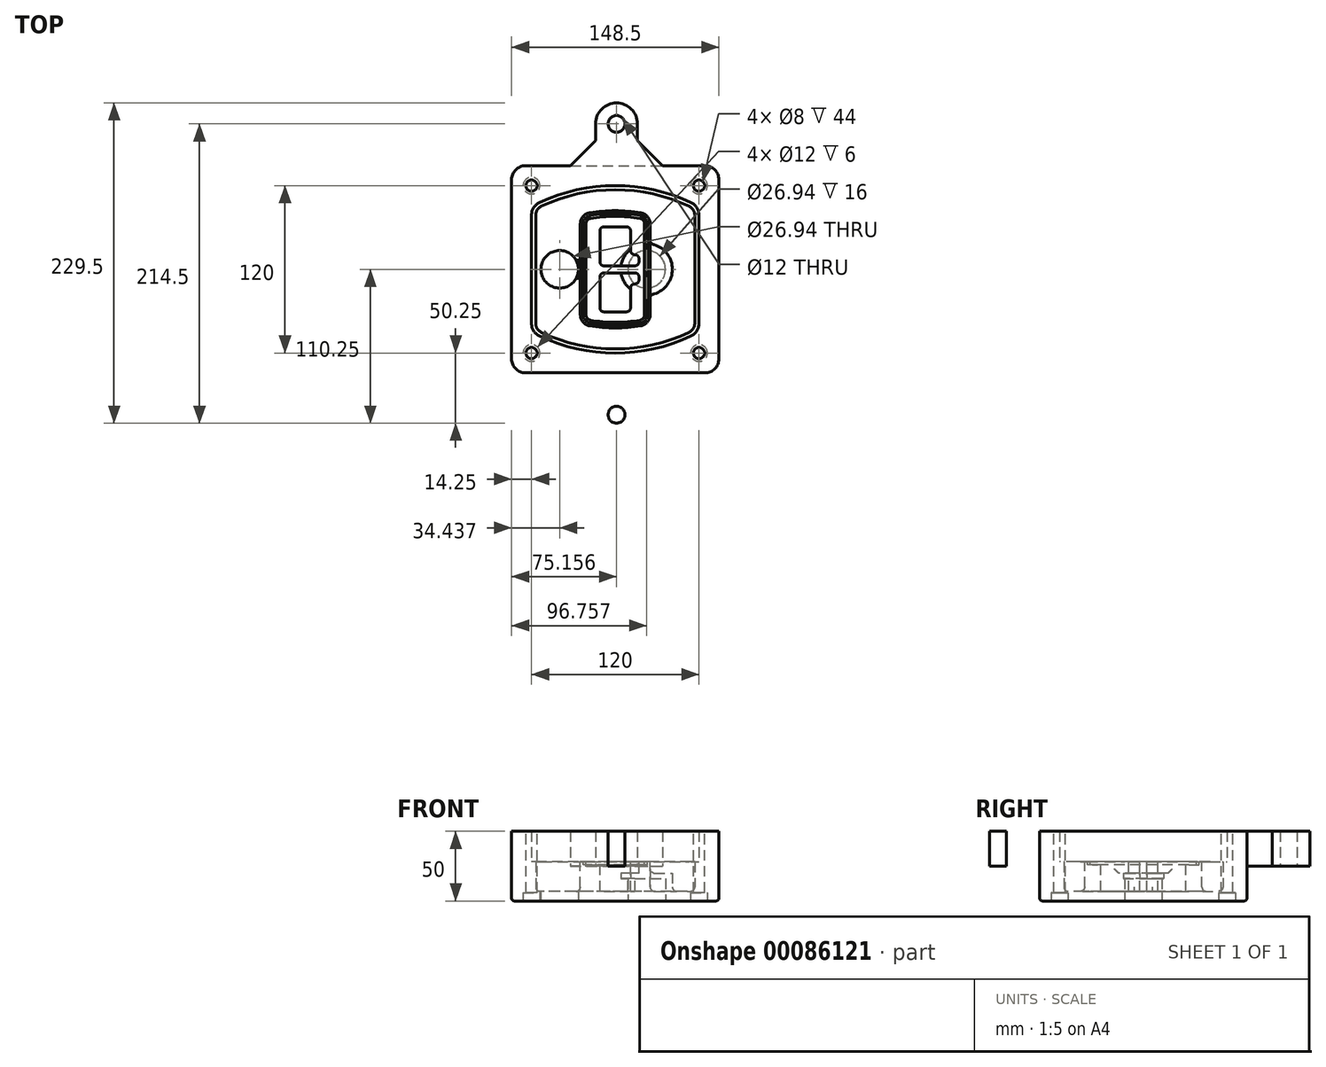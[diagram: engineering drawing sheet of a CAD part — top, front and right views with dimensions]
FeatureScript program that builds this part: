
annotation { "Feature Type Name" : "Feature", "Feature Type Description" : "" }
export const myFeature = defineFeature(function(context is Context, id is Id, definition is map)
    precondition{}
    {
        {
            var Q0;
            Q0=qCreatedBy(makeId("Top.planeOp"),FACE);
            var sketch = newSketch(context, id + "F0", { "sketchPlane" : qUnion([Q0])});
            skPoint(sketch, "E0.rect.middle", {"position": v(0, 0) * mm});
            skLineSegment(sketch, "E1.bottom", {"start": v(-64.25, -74.25) * mm, "end": v(64.25, -74.25) * mm});
            skLineSegment(sketch, "E1.top", {"start": v(-64.25, 74.25) * mm, "end": v(64.25, 74.25) * mm});
            skLineSegment(sketch, "E1.left", {"start": v(-74.25, -64.25) * mm, "end": v(-74.25, 64.25) * mm});
            skLineSegment(sketch, "E1.right", {"start": v(74.25, -64.25) * mm, "end": v(74.25, 64.25) * mm});
            skLineSegment(sketch, "E2", {"start": v(-74.25, 74.25) * mm, "end": v(74.25, -74.25) * mm, "construction": true});
            skLineSegment(sketch, "E3", {"start": v(74.25, 74.25) * mm, "end": v(-74.25, -74.25) * mm, "construction": true});
            skCircle(sketch, "E4", {"center": v(-60, 60) * mm, "radius": 4 * mm});
            skCircle(sketch, "E5", {"center": v(60, 60) * mm, "radius": 4 * mm});
            skCircle(sketch, "E6", {"center": v(60, -60) * mm, "radius": 4 * mm});
            skCircle(sketch, "E7", {"center": v(-60, -60) * mm, "radius": 4 * mm});
            skLineSegment(sketch, "E8", {"start": v(-60, 60) * mm, "end": v(60, 60) * mm, "construction": true});
            skLineSegment(sketch, "E9", {"start": v(60, 60) * mm, "end": v(60, -60) * mm, "construction": true});
            skLineSegment(sketch, "E10", {"start": v(60, -60) * mm, "end": v(-60, -60) * mm, "construction": true});
            skLineSegment(sketch, "E11", {"start": v(-60, -60) * mm, "end": v(-60, 60) * mm, "construction": true});
            skLineSegment(sketch, "E12", {"start": v(-60, 38.83) * mm, "end": v(-60, -38.83) * mm});
            skLineSegment(sketch, "E13", {"start": v(60, 38.83) * mm, "end": v(60, -38.83) * mm});
            skArc(sketch, "E14", {"start": v(54.26, 47.88) * mm, "mid": v(0, 60) * mm, "end": v(-54.26, 47.88) * mm});
            skArc(sketch, "E15", {"start": v(-54.26, -47.88) * mm, "mid": v(0, -60) * mm, "end": v(54.26, -47.88) * mm});
            skLineSegment(sketch, "E16", {"start": v(-60, 0) * mm, "end": v(60, 0) * mm, "construction": true});
            skPoint(sketch, "E17.visualSharp", {"position": v(-60, -45) * mm});
            skArc(sketch, "E17.filletArc", {"start": v(-60, -38.83) * mm, "mid": v(-58.44, -44.2) * mm, "end": v(-54.26, -47.88) * mm});
            skPoint(sketch, "E18.visualSharp", {"position": v(-60, 45) * mm});
            skArc(sketch, "E18.filletArc", {"start": v(-54.26, 47.88) * mm, "mid": v(-58.44, 44.2) * mm, "end": v(-60, 38.83) * mm});
            skPoint(sketch, "E19.visualSharp", {"position": v(60, 45) * mm});
            skArc(sketch, "E19.filletArc", {"start": v(60, 38.83) * mm, "mid": v(58.44, 44.2) * mm, "end": v(54.26, 47.88) * mm});
            skPoint(sketch, "E20.visualSharp", {"position": v(60, -45) * mm});
            skArc(sketch, "E20.filletArc", {"start": v(54.26, -47.88) * mm, "mid": v(58.44, -44.2) * mm, "end": v(60, -38.83) * mm});
            skPoint(sketch, "E21.visualSharp", {"position": v(-74.25, 74.25) * mm});
            skArc(sketch, "E21.filletArc", {"start": v(-64.25, 74.25) * mm, "mid": v(-71.32, 71.32) * mm, "end": v(-74.25, 64.25) * mm});
            skPoint(sketch, "E22.visualSharp", {"position": v(74.25, 74.25) * mm});
            skArc(sketch, "E22.filletArc", {"start": v(74.25, 64.25) * mm, "mid": v(71.32, 71.32) * mm, "end": v(64.25, 74.25) * mm});
            skPoint(sketch, "E23.visualSharp", {"position": v(74.25, -74.25) * mm});
            skArc(sketch, "E23.filletArc", {"start": v(64.25, -74.25) * mm, "mid": v(71.32, -71.32) * mm, "end": v(74.25, -64.25) * mm});
            skPoint(sketch, "E24.visualSharp", {"position": v(-74.25, -74.25) * mm});
            skArc(sketch, "E24.filletArc", {"start": v(-74.25, -64.25) * mm, "mid": v(-71.32, -71.32) * mm, "end": v(-64.25, -74.25) * mm});
            skArc(sketch, "E25.0", {"start": v(57, 38.83) * mm, "mid": v(55.9, 42.58) * mm, "end": v(52.98, 45.17) * mm});
            skLineSegment(sketch, "E25.1", {"start": v(57, 38.83) * mm, "end": v(57, -38.83) * mm});
            skArc(sketch, "E25.2", {"start": v(52.98, -45.17) * mm, "mid": v(55.9, -42.58) * mm, "end": v(57, -38.83) * mm});
            skArc(sketch, "E25.3", {"start": v(-52.98, -45.17) * mm, "mid": v(0, -57) * mm, "end": v(52.98, -45.17) * mm});
            skArc(sketch, "E25.4", {"start": v(-57, -38.83) * mm, "mid": v(-55.9, -42.58) * mm, "end": v(-52.98, -45.17) * mm});
            skArc(sketch, "E25.5", {"start": v(52.98, 45.17) * mm, "mid": v(0, 57) * mm, "end": v(-52.98, 45.17) * mm});
            skLineSegment(sketch, "E25.6", {"start": v(-57, 38.83) * mm, "end": v(-57, -38.83) * mm});
            skArc(sketch, "E25.7", {"start": v(-52.98, 45.17) * mm, "mid": v(-55.9, 42.58) * mm, "end": v(-57, 38.83) * mm});
            skArc(sketch, "E26.0", {"start": v(-55.96, 51.5) * mm, "mid": v(-61.82, 46.33) * mm, "end": v(-64, 38.83) * mm});
            skArc(sketch, "E26.1", {"start": v(55.96, 51.5) * mm, "mid": v(0, 64) * mm, "end": v(-55.96, 51.5) * mm});
            skArc(sketch, "E26.2", {"start": v(64, 38.83) * mm, "mid": v(61.82, 46.33) * mm, "end": v(55.96, 51.5) * mm});
            skLineSegment(sketch, "E26.3", {"start": v(64, 38.83) * mm, "end": v(64, -38.83) * mm});
            skArc(sketch, "E26.4", {"start": v(55.96, -51.5) * mm, "mid": v(61.82, -46.33) * mm, "end": v(64, -38.83) * mm});
            skLineSegment(sketch, "E26.5", {"start": v(-64, 38.83) * mm, "end": v(-64, -38.83) * mm});
            skArc(sketch, "E26.6", {"start": v(-55.96, -51.5) * mm, "mid": v(0, -64) * mm, "end": v(55.96, -51.5) * mm});
            skArc(sketch, "E26.7", {"start": v(-64, -38.83) * mm, "mid": v(-61.82, -46.33) * mm, "end": v(-55.96, -51.5) * mm});
            skSolve(sketch);
        }
        {
            var Q0;
            Q0=makeQuery(id+"F0.imprint","IMPRINT",FACE,{"disambiguationData":[TD([[makeQuery(id+"F0.imprint","IMPRINT",EDGE,{"derivedFrom":sQuery(id+"F0.wireOp",EDGE,"E1.bottom")}),1.0]])]});
            var Q1;
            Q1=makeQuery(id+"F0.imprint","IMPRINT",FACE,{"disambiguationData":[TD([[makeQuery(id+"F0.imprint","IMPRINT",EDGE,{"derivedFrom":sQuery(id+"F0.wireOp",EDGE,"E12")}),1.0]])]});
            var Q2;
            Q2=makeQuery(id+"F0.imprint","IMPRINT",FACE,{"disambiguationData":[TD([[makeQuery(id+"F0.imprint","IMPRINT",EDGE,{"derivedFrom":sQuery(id+"F0.wireOp",EDGE,"E25.0")}),1.0]])]});
            var Q3;
            Q3=makeQuery(id+"F0.imprint","IMPRINT",FACE,{"disambiguationData":[TD([[makeQuery(id+"F0.imprint","IMPRINT",EDGE,{"derivedFrom":sQuery(id+"F0.wireOp",EDGE,"E12")}),-1.0]])]});
            extrude(context, id + "F1", {"entities" : qUnion([Q0, Q1, Q2, Q3]), "oppositeDirection" : true, "depth" : 25 * mm});
        }
        {
            var Q0;
            Q0=makeQuery(id+"F0.imprint","IMPRINT",FACE,{"disambiguationData":[TD([[makeQuery(id+"F0.imprint","IMPRINT",EDGE,{"derivedFrom":sQuery(id+"F0.wireOp",EDGE,"E12")}),1.0]])]});
            extrude(context, id + "F2", {"entities" : qUnion([Q0]), "operationType" : NewBodyOperationType.ADD, "depth" : 3 * mm});
        }
        {
            var Q0;
            Q0=makeQuery(id+"F0.imprint","IMPRINT",FACE,{"disambiguationData":[TD([[makeQuery(id+"F0.imprint","IMPRINT",EDGE,{"derivedFrom":sQuery(id+"F0.wireOp",EDGE,"E25.0")}),1.0]])]});
            extrude(context, id + "F3", {"entities" : qUnion([Q0]), "operationType" : NewBodyOperationType.REMOVE, "oppositeDirection" : true, "depth" : 18 * mm});
        }
        {
            var Q0;
            Q0=makeQuery(id+"F2.opExtrude","CAP_FACE",FACE,{"disambiguationData":[OSD([sQuery(id+"F0.wireOp",EDGE,"E12"),sQuery(id+"F0.wireOp",EDGE,"E13"),sQuery(id+"F0.wireOp",EDGE,"E14"),sQuery(id+"F0.wireOp",EDGE,"E15"),sQuery(id+"F0.wireOp",EDGE,"E17.filletArc"),sQuery(id+"F0.wireOp",EDGE,"E18.filletArc"),sQuery(id+"F0.wireOp",EDGE,"E19.filletArc"),sQuery(id+"F0.wireOp",EDGE,"E20.filletArc"),sQuery(id+"F0.wireOp",EDGE,"E25.0"),sQuery(id+"F0.wireOp",EDGE,"E25.1"),sQuery(id+"F0.wireOp",EDGE,"E25.2"),sQuery(id+"F0.wireOp",EDGE,"E25.3"),sQuery(id+"F0.wireOp",EDGE,"E25.4"),sQuery(id+"F0.wireOp",EDGE,"E25.5"),sQuery(id+"F0.wireOp",EDGE,"E25.6"),sQuery(id+"F0.wireOp",EDGE,"E25.7")])],"isStart":false});
            var sketch = newSketch(context, id + "F4", { "sketchPlane" : qUnion([Q0])});
            skArc(sketch, "E27.0", {"start": v(-18.34, -40.45) * mm, "mid": v(0, -42) * mm, "end": v(18.34, -40.45) * mm});
            skArc(sketch, "E28.0", {"start": v(18.34, 40.45) * mm, "mid": v(0, 42) * mm, "end": v(-18.34, 40.45) * mm});
            skLineSegment(sketch, "E29", {"start": v(-25, 32.57) * mm, "end": v(-25, -32.57) * mm});
            skLineSegment(sketch, "E30", {"start": v(25, 32.57) * mm, "end": v(25, -32.57) * mm});
            skLineSegment(sketch, "E31", {"start": v(-25, 39.1) * mm, "end": v(25, 39.1) * mm, "construction": true});
            skLineSegment(sketch, "E32", {"start": v(-25, -39.1) * mm, "end": v(25, -39.1) * mm, "construction": true});
            skPoint(sketch, "E33.visualSharp", {"position": v(-25, 39.1) * mm});
            skArc(sketch, "E33.filletArc", {"start": v(-18.34, 40.45) * mm, "mid": v(-23.11, 37.73) * mm, "end": v(-25, 32.57) * mm});
            skPoint(sketch, "E34.visualSharp", {"position": v(25, 39.1) * mm});
            skArc(sketch, "E34.filletArc", {"start": v(25, 32.57) * mm, "mid": v(23.11, 37.73) * mm, "end": v(18.34, 40.45) * mm});
            skPoint(sketch, "E35.visualSharp", {"position": v(25, -39.1) * mm});
            skArc(sketch, "E35.filletArc", {"start": v(18.34, -40.45) * mm, "mid": v(23.11, -37.73) * mm, "end": v(25, -32.57) * mm});
            skPoint(sketch, "E36.visualSharp", {"position": v(-25, -39.1) * mm});
            skArc(sketch, "E36.filletArc", {"start": v(-25, -32.57) * mm, "mid": v(-23.11, -37.73) * mm, "end": v(-18.34, -40.45) * mm});
            skArc(sketch, "E37.0", {"start": v(52.98, 45.17) * mm, "mid": v(0, 57) * mm, "end": v(-52.98, 45.17) * mm});
            skArc(sketch, "E37.1", {"start": v(-52.98, 45.17) * mm, "mid": v(-55.9, 42.58) * mm, "end": v(-57, 38.83) * mm});
            skLineSegment(sketch, "E37.2", {"start": v(-57, 38.83) * mm, "end": v(-57, -38.83) * mm});
            skArc(sketch, "E37.3", {"start": v(-57, -38.83) * mm, "mid": v(-55.9, -42.58) * mm, "end": v(-52.98, -45.17) * mm});
            skArc(sketch, "E37.4", {"start": v(-52.98, -45.17) * mm, "mid": v(0, -57) * mm, "end": v(52.98, -45.17) * mm});
            skArc(sketch, "E37.5", {"start": v(52.98, -45.17) * mm, "mid": v(55.9, -42.58) * mm, "end": v(57, -38.83) * mm});
            skLineSegment(sketch, "E37.6", {"start": v(57, 38.83) * mm, "end": v(57, -38.83) * mm});
            skArc(sketch, "E37.7", {"start": v(57, 38.83) * mm, "mid": v(55.9, 42.58) * mm, "end": v(52.98, 45.17) * mm});
            skLineSegment(sketch, "E38.0", {"start": v(23, 32.57) * mm, "end": v(23, -32.57) * mm});
            skArc(sketch, "E38.1", {"start": v(18, -38.48) * mm, "mid": v(21.58, -36.44) * mm, "end": v(23, -32.57) * mm});
            skArc(sketch, "E38.2", {"start": v(-18, -38.48) * mm, "mid": v(0, -40) * mm, "end": v(18, -38.48) * mm});
            skArc(sketch, "E38.3", {"start": v(-23, -32.57) * mm, "mid": v(-21.58, -36.44) * mm, "end": v(-18, -38.48) * mm});
            skLineSegment(sketch, "E38.4", {"start": v(-23, 32.57) * mm, "end": v(-23, -32.57) * mm});
            skArc(sketch, "E38.5", {"start": v(23, 32.57) * mm, "mid": v(21.58, 36.44) * mm, "end": v(18, 38.48) * mm});
            skArc(sketch, "E38.6", {"start": v(-18, 38.48) * mm, "mid": v(-21.58, 36.44) * mm, "end": v(-23, 32.57) * mm});
            skArc(sketch, "E38.7", {"start": v(18, 38.48) * mm, "mid": v(0, 40) * mm, "end": v(-18, 38.48) * mm});
            skArc(sketch, "E39.0", {"start": v(21, 32.57) * mm, "mid": v(20.06, 35.15) * mm, "end": v(17.67, 36.5) * mm});
            skLineSegment(sketch, "E39.1", {"start": v(21, 32.57) * mm, "end": v(21, -32.57) * mm});
            skArc(sketch, "E39.2", {"start": v(17.67, -36.5) * mm, "mid": v(20.06, -35.15) * mm, "end": v(21, -32.57) * mm});
            skArc(sketch, "E39.3", {"start": v(-17.67, -36.5) * mm, "mid": v(0, -38) * mm, "end": v(17.67, -36.5) * mm});
            skArc(sketch, "E39.4", {"start": v(-21, -32.57) * mm, "mid": v(-20.06, -35.15) * mm, "end": v(-17.67, -36.5) * mm});
            skArc(sketch, "E39.5", {"start": v(17.67, 36.5) * mm, "mid": v(0, 38) * mm, "end": v(-17.67, 36.5) * mm});
            skLineSegment(sketch, "E39.6", {"start": v(-21, 32.57) * mm, "end": v(-21, -32.57) * mm});
            skArc(sketch, "E39.7", {"start": v(-17.67, 36.5) * mm, "mid": v(-20.06, 35.15) * mm, "end": v(-21, 32.57) * mm});
            skLineSegment(sketch, "E40", {"start": v(-25, 0) * mm, "end": v(25, 0) * mm, "construction": true});
            skLineSegment(sketch, "E41", {"start": v(-11, 5.5) * mm, "end": v(-11, 27.5) * mm});
            skLineSegment(sketch, "E42", {"start": v(-8, 30.5) * mm, "end": v(8, 30.5) * mm});
            skLineSegment(sketch, "E43", {"start": v(11, 27.5) * mm, "end": v(11, 13.5) * mm});
            skLineSegment(sketch, "E44", {"start": v(14, 10.5) * mm, "end": v(14, 10.5) * mm});
            skLineSegment(sketch, "E45", {"start": v(17, 7.5) * mm, "end": v(17, 5.5) * mm});
            skLineSegment(sketch, "E46", {"start": v(14, 2.5) * mm, "end": v(-8, 2.5) * mm});
            skPoint(sketch, "E47.visualSharp", {"position": v(-11, 30.5) * mm});
            skArc(sketch, "E47.filletArc", {"start": v(-8, 30.5) * mm, "mid": v(-10.12, 29.62) * mm, "end": v(-11, 27.5) * mm});
            skPoint(sketch, "E48.visualSharp", {"position": v(11, 30.5) * mm});
            skArc(sketch, "E48.filletArc", {"start": v(11, 27.5) * mm, "mid": v(10.12, 29.62) * mm, "end": v(8, 30.5) * mm});
            skPoint(sketch, "E49.visualSharp", {"position": v(11, 10.5) * mm});
            skArc(sketch, "E49.filletArc", {"start": v(11, 13.5) * mm, "mid": v(11.88, 11.38) * mm, "end": v(14, 10.5) * mm});
            skPoint(sketch, "E50.visualSharp", {"position": v(17, 10.5) * mm});
            skArc(sketch, "E50.filletArc", {"start": v(17, 7.5) * mm, "mid": v(16.12, 9.62) * mm, "end": v(14, 10.5) * mm});
            skPoint(sketch, "E51.visualSharp", {"position": v(17, 2.5) * mm});
            skArc(sketch, "E51.filletArc", {"start": v(14, 2.5) * mm, "mid": v(16.12, 3.38) * mm, "end": v(17, 5.5) * mm});
            skPoint(sketch, "E52.visualSharp", {"position": v(-11, 2.5) * mm});
            skArc(sketch, "E52.filletArc", {"start": v(-11, 5.5) * mm, "mid": v(-10.12, 3.38) * mm, "end": v(-8, 2.5) * mm});
            skLineSegment(sketch, "E53.0.MirrorCS", {"start": v(14, -2.5) * mm, "end": v(-8, -2.5) * mm});
            skArc(sketch, "E54.0.MirrorCS", {"start": v(-11, -5.5) * mm, "mid": v(-10.12, -3.38) * mm, "end": v(-8, -2.5) * mm});
            skLineSegment(sketch, "E55.0.MirrorCS", {"start": v(-11, -5.5) * mm, "end": v(-11, -27.5) * mm});
            skArc(sketch, "E56.0.MirrorCS", {"start": v(-8, -30.5) * mm, "mid": v(-10.12, -29.62) * mm, "end": v(-11, -27.5) * mm});
            skLineSegment(sketch, "E57.0.MirrorCS", {"start": v(-8, -30.5) * mm, "end": v(8, -30.5) * mm});
            skArc(sketch, "E58.0.MirrorCS", {"start": v(11, -27.5) * mm, "mid": v(10.12, -29.62) * mm, "end": v(8, -30.5) * mm});
            skLineSegment(sketch, "E59.0.MirrorCS", {"start": v(11, -27.5) * mm, "end": v(11, -13.5) * mm});
            skArc(sketch, "E60.0.MirrorCS", {"start": v(11, -13.5) * mm, "mid": v(11.88, -11.38) * mm, "end": v(14, -10.5) * mm});
            skArc(sketch, "E61.0.MirrorCS", {"start": v(17, -7.5) * mm, "mid": v(16.12, -9.62) * mm, "end": v(14, -10.5) * mm});
            skLineSegment(sketch, "E62.0.MirrorCS", {"start": v(17, -7.5) * mm, "end": v(17, -5.5) * mm});
            skArc(sketch, "E63.0.MirrorCS", {"start": v(14, -2.5) * mm, "mid": v(16.12, -3.38) * mm, "end": v(17, -5.5) * mm});
            skSolve(sketch);
        }
        {
            var Q0;
            Q0=makeQuery(id+"F4.imprint","IMPRINT",FACE,{"disambiguationData":[TD([[makeQuery(id+"F4.imprint","IMPRINT",EDGE,{"derivedFrom":sQuery(id+"F4.wireOp",EDGE,"E27.0")}),1.0]])]});
            var Q1;
            Q1=makeQuery(id+"F4.imprint","IMPRINT",FACE,{"disambiguationData":[TD([[makeQuery(id+"F4.imprint","IMPRINT",EDGE,{"derivedFrom":sQuery(id+"F4.wireOp",EDGE,"E38.0")}),-1.0]])]});
            var Q2;
            Q2=makeQuery(id+"F4.imprint","IMPRINT",FACE,{"disambiguationData":[TD([[makeQuery(id+"F4.imprint","IMPRINT",EDGE,{"derivedFrom":sQuery(id+"F4.wireOp",EDGE,"E39.0")}),1.0]])]});
            extrude(context, id + "F5", {"entities" : qUnion([Q0, Q1, Q2]), "operationType" : NewBodyOperationType.ADD, "endBound" : BoundingType.UP_TO_NEXT, "oppositeDirection" : true, "depth" : 25 * mm});
        }
        {
            var Q0;
            Q0=makeQuery(id+"F4.imprint","IMPRINT",FACE,{"disambiguationData":[TD([[makeQuery(id+"F4.imprint","IMPRINT",EDGE,{"derivedFrom":sQuery(id+"F4.wireOp",EDGE,"E38.0")}),-1.0]])]});
            extrude(context, id + "F6", {"entities" : qUnion([Q0]), "operationType" : NewBodyOperationType.REMOVE, "oppositeDirection" : true, "depth" : 2 * mm});
        }
        {
            var Q0;
            Q0=makeQuery(id+"F1.opExtrude","CAP_FACE",FACE,{"disambiguationData":[OSD([sQuery(id+"F0.wireOp",EDGE,"E1.bottom"),sQuery(id+"F0.wireOp",EDGE,"E1.top"),sQuery(id+"F0.wireOp",EDGE,"E1.left"),sQuery(id+"F0.wireOp",EDGE,"E1.right"),sQuery(id+"F0.wireOp",EDGE,"E4"),sQuery(id+"F0.wireOp",EDGE,"E5"),sQuery(id+"F0.wireOp",EDGE,"E6"),sQuery(id+"F0.wireOp",EDGE,"E7"),sQuery(id+"F0.wireOp",EDGE,"E21.filletArc"),sQuery(id+"F0.wireOp",EDGE,"E22.filletArc"),sQuery(id+"F0.wireOp",EDGE,"E23.filletArc"),sQuery(id+"F0.wireOp",EDGE,"E24.filletArc")])],"isStart":false});
            var sketch = newSketch(context, id + "F7", { "sketchPlane" : qUnion([Q0])});
            skCircle(sketch, "E64", {"center": v(22.5, 0) * mm, "radius": 13.47 * mm});
            skCircle(sketch, "E65", {"center": v(-39.81, 0) * mm, "radius": 13.47 * mm});
            skLineSegment(sketch, "E66", {"start": v(74.25, 0) * mm, "end": v(-74.25, 0) * mm});
            skCircle(sketch, "E67", {"center": v(22.5, 0) * mm, "radius": 18.47 * mm});
            skCircle(sketch, "E68", {"center": v(60, -60) * mm, "radius": 6 * mm});
            skCircle(sketch, "E69", {"center": v(-60, -60) * mm, "radius": 6 * mm});
            skCircle(sketch, "E70", {"center": v(-60, 60) * mm, "radius": 6 * mm});
            skCircle(sketch, "E71", {"center": v(60, 60) * mm, "radius": 6 * mm});
            skSolve(sketch);
        }
        {
            var Q0;
            {var subQ1=sQuery(id+"F7.wireOp",EDGE,"E66");var subQ4=sQuery(id+"F7.wireOp",EDGE,"E64");var subQ6=makeQuery(id+"F7.imprint","INTERSECT",VERTEX,{"disambiguationData":[OD(0.0)],"derivedFrom":[subQ4,subQ1]});Q0=makeQuery(id+"F7.imprint","IMPRINT",FACE,{"disambiguationData":[TD([[makeQuery(id+"F7.imprint","IMPRINT",EDGE,{"disambiguationData":[TD([[subQ6,-1.0]])],"derivedFrom":subQ4}),-1.0]])]});}
            var Q1;
            {var subQ0=sQuery(id+"F7.wireOp",EDGE,"E66");var subQ1=sQuery(id+"F7.wireOp",EDGE,"E64");var subQ3=makeQuery(id+"F7.imprint","INTERSECT",VERTEX,{"disambiguationData":[OD(0.0)],"derivedFrom":[subQ1,subQ0]});Q1=makeQuery(id+"F7.imprint","IMPRINT",FACE,{"disambiguationData":[TD([[makeQuery(id+"F7.imprint","IMPRINT",EDGE,{"disambiguationData":[TD([[subQ3,-1.0]])],"derivedFrom":subQ1}),1.0]])]});}
            var Q2;
            {var subQ0=sQuery(id+"F7.wireOp",EDGE,"E66");var subQ1=sQuery(id+"F7.wireOp",EDGE,"E64");var subQ3=makeQuery(id+"F7.imprint","INTERSECT",VERTEX,{"disambiguationData":[OD(0.0)],"derivedFrom":[subQ1,subQ0]});Q2=makeQuery(id+"F7.imprint","IMPRINT",FACE,{"disambiguationData":[TD([[makeQuery(id+"F7.imprint","IMPRINT",EDGE,{"disambiguationData":[TD([[subQ3,1.0]])],"derivedFrom":subQ1}),1.0]])]});}
            var Q3;
            {var subQ1=sQuery(id+"F7.wireOp",EDGE,"E66");var subQ4=sQuery(id+"F7.wireOp",EDGE,"E64");var subQ6=makeQuery(id+"F7.imprint","INTERSECT",VERTEX,{"disambiguationData":[OD(0.0)],"derivedFrom":[subQ4,subQ1]});Q3=makeQuery(id+"F7.imprint","IMPRINT",FACE,{"disambiguationData":[TD([[makeQuery(id+"F7.imprint","IMPRINT",EDGE,{"disambiguationData":[TD([[subQ6,1.0]])],"derivedFrom":subQ4}),-1.0]])]});}
            extrude(context, id + "F8", {"entities" : qUnion([Q0, Q1, Q2, Q3]), "operationType" : NewBodyOperationType.ADD, "oppositeDirection" : true, "depth" : 20 * mm});
        }
        {
            var Q0;
            {var subQ0=sQuery(id+"F7.wireOp",EDGE,"E66");var subQ1=sQuery(id+"F7.wireOp",EDGE,"E64");var subQ3=makeQuery(id+"F7.imprint","INTERSECT",VERTEX,{"disambiguationData":[OD(0.0)],"derivedFrom":[subQ1,subQ0]});Q0=makeQuery(id+"F7.imprint","IMPRINT",FACE,{"disambiguationData":[TD([[makeQuery(id+"F7.imprint","IMPRINT",EDGE,{"disambiguationData":[TD([[subQ3,-1.0]])],"derivedFrom":subQ1}),1.0]])]});}
            var Q1;
            {var subQ0=sQuery(id+"F7.wireOp",EDGE,"E66");var subQ1=sQuery(id+"F7.wireOp",EDGE,"E64");var subQ3=makeQuery(id+"F7.imprint","INTERSECT",VERTEX,{"disambiguationData":[OD(0.0)],"derivedFrom":[subQ1,subQ0]});Q1=makeQuery(id+"F7.imprint","IMPRINT",FACE,{"disambiguationData":[TD([[makeQuery(id+"F7.imprint","IMPRINT",EDGE,{"disambiguationData":[TD([[subQ3,1.0]])],"derivedFrom":subQ1}),1.0]])]});}
            extrude(context, id + "F9", {"entities" : qUnion([Q0, Q1]), "operationType" : NewBodyOperationType.REMOVE, "oppositeDirection" : true, "depth" : 16 * mm});
        }
        {
            var Q0;
            {var subQ0=sQuery(id+"F7.wireOp",EDGE,"E66");var subQ1=sQuery(id+"F7.wireOp",EDGE,"E65");var subQ3=makeQuery(id+"F7.imprint","INTERSECT",VERTEX,{"disambiguationData":[OD(0.0)],"derivedFrom":[subQ1,subQ0]});Q0=makeQuery(id+"F7.imprint","IMPRINT",FACE,{"disambiguationData":[TD([[makeQuery(id+"F7.imprint","IMPRINT",EDGE,{"disambiguationData":[TD([[subQ3,-1.0]])],"derivedFrom":subQ1}),1.0]])]});}
            var Q1;
            {var subQ0=sQuery(id+"F7.wireOp",EDGE,"E66");var subQ1=sQuery(id+"F7.wireOp",EDGE,"E65");var subQ3=makeQuery(id+"F7.imprint","INTERSECT",VERTEX,{"disambiguationData":[OD(0.0)],"derivedFrom":[subQ1,subQ0]});Q1=makeQuery(id+"F7.imprint","IMPRINT",FACE,{"disambiguationData":[TD([[makeQuery(id+"F7.imprint","IMPRINT",EDGE,{"disambiguationData":[TD([[subQ3,1.0]])],"derivedFrom":subQ1}),1.0]])]});}
            extrude(context, id + "F10", {"entities" : qUnion([Q0, Q1]), "operationType" : NewBodyOperationType.REMOVE, "oppositeDirection" : true, "depth" : 25 * mm});
        }
        {
            var Q0;
            Q0=makeQuery(id+"F7.imprint","IMPRINT",FACE,{"disambiguationData":[TD([[makeQuery(id+"F7.imprint","IMPRINT",EDGE,{"derivedFrom":sQuery(id+"F7.wireOp",EDGE,"E68")}),1.0]])]});
            var Q1;
            Q1=makeQuery(id+"F7.imprint","IMPRINT",FACE,{"disambiguationData":[TD([[makeQuery(id+"F7.imprint","IMPRINT",EDGE,{"derivedFrom":makeQuery(id+"F1.opExtrude","CAP_EDGE",EDGE,{"disambiguationData":[OSD([sQuery(id+"F0.wireOp",EDGE,"E5")])],"isStart":false})}),-1.0]])]});
            var Q2;
            Q2=makeQuery(id+"F7.imprint","IMPRINT",FACE,{"disambiguationData":[TD([[makeQuery(id+"F7.imprint","IMPRINT",EDGE,{"derivedFrom":sQuery(id+"F7.wireOp",EDGE,"E69")}),1.0]])]});
            var Q3;
            Q3=makeQuery(id+"F7.imprint","IMPRINT",FACE,{"disambiguationData":[TD([[makeQuery(id+"F7.imprint","IMPRINT",EDGE,{"derivedFrom":makeQuery(id+"F1.opExtrude","CAP_EDGE",EDGE,{"disambiguationData":[OSD([sQuery(id+"F0.wireOp",EDGE,"E4")])],"isStart":false})}),-1.0]])]});
            var Q4;
            Q4=makeQuery(id+"F7.imprint","IMPRINT",FACE,{"disambiguationData":[TD([[makeQuery(id+"F7.imprint","IMPRINT",EDGE,{"derivedFrom":sQuery(id+"F7.wireOp",EDGE,"E70")}),1.0]])]});
            var Q5;
            Q5=makeQuery(id+"F7.imprint","IMPRINT",FACE,{"disambiguationData":[TD([[makeQuery(id+"F7.imprint","IMPRINT",EDGE,{"derivedFrom":makeQuery(id+"F1.opExtrude","CAP_EDGE",EDGE,{"disambiguationData":[OSD([sQuery(id+"F0.wireOp",EDGE,"E7")])],"isStart":false})}),-1.0]])]});
            var Q6;
            Q6=makeQuery(id+"F7.imprint","IMPRINT",FACE,{"disambiguationData":[TD([[makeQuery(id+"F7.imprint","IMPRINT",EDGE,{"derivedFrom":sQuery(id+"F7.wireOp",EDGE,"E71")}),1.0]])]});
            var Q7;
            Q7=makeQuery(id+"F7.imprint","IMPRINT",FACE,{"disambiguationData":[TD([[makeQuery(id+"F7.imprint","IMPRINT",EDGE,{"derivedFrom":makeQuery(id+"F1.opExtrude","CAP_EDGE",EDGE,{"disambiguationData":[OSD([sQuery(id+"F0.wireOp",EDGE,"E6")])],"isStart":false})}),-1.0]])]});
            extrude(context, id + "F11", {"entities" : qUnion([Q0, Q1, Q2, Q3, Q4, Q5, Q6, Q7]), "operationType" : NewBodyOperationType.REMOVE, "oppositeDirection" : true, "depth" : 6 * mm});
        }
        {
            var Q0;
            Q0=makeQuery(id+"F9.boolean.opBoolean","COPY",FACE,{"derivedFrom":makeQuery(id+"F9.opExtrude","CAP_FACE",FACE,{"disambiguationData":[OSD([sQuery(id+"F7.wireOp",EDGE,"E64")])],"isStart":false})});
            var sketch = newSketch(context, id + "F12", { "sketchPlane" : qUnion([Q0])});
            skArc(sketch, "E72.0", {"start": v(11, 14.45) * mm, "mid": v(6.45, 9.13) * mm, "end": v(4.2, 2.5) * mm});
            skArc(sketch, "E72.1", {"start": v(4.2, -2.5) * mm, "mid": v(6.45, -9.13) * mm, "end": v(11, -14.45) * mm});
            skLineSegment(sketch, "E73", {"start": v(4.2, -2.5) * mm, "end": v(14, -2.5) * mm});
            skLineSegment(sketch, "E74.0", {"start": v(14, 2.5) * mm, "end": v(4.2, 2.5) * mm});
            skArc(sketch, "E74.1", {"start": v(14, 2.5) * mm, "mid": v(16.12, 3.38) * mm, "end": v(17, 5.5) * mm});
            skLineSegment(sketch, "E74.2", {"start": v(17, 7.5) * mm, "end": v(17, 5.5) * mm});
            skArc(sketch, "E74.3", {"start": v(17, 7.5) * mm, "mid": v(16.12, 9.62) * mm, "end": v(14, 10.5) * mm});
            skArc(sketch, "E74.4", {"start": v(11, 13.5) * mm, "mid": v(11.88, 11.38) * mm, "end": v(14, 10.5) * mm});
            skLineSegment(sketch, "E74.5", {"start": v(11, 14.45) * mm, "end": v(11, 13.5) * mm});
            skLineSegment(sketch, "E74.7", {"start": v(14, -2.5) * mm, "end": v(4.2, -2.5) * mm});
            skArc(sketch, "E74.8", {"start": v(14, -2.5) * mm, "mid": v(16.12, -3.38) * mm, "end": v(17, -5.5) * mm});
            skLineSegment(sketch, "E74.9", {"start": v(17, -7.5) * mm, "end": v(17, -5.5) * mm});
            skArc(sketch, "E74.10", {"start": v(17, -7.5) * mm, "mid": v(16.12, -9.62) * mm, "end": v(14, -10.5) * mm});
            skArc(sketch, "E74.11", {"start": v(11, -13.5) * mm, "mid": v(11.88, -11.38) * mm, "end": v(14, -10.5) * mm});
            skLineSegment(sketch, "E74.12", {"start": v(11, -14.45) * mm, "end": v(11, -13.5) * mm});
            skPoint(sketch, "E75.orphan", {"position": v(11, -27.5) * mm});
            skPoint(sketch, "E76.orphan", {"position": v(-8, -2.5) * mm});
            skPoint(sketch, "E77.orphan", {"position": v(-8, 2.5) * mm});
            skPoint(sketch, "E78.orphan", {"position": v(11, 27.5) * mm});
            skSolve(sketch);
        }
        {
            var Q0;
            {var subQ7=sQuery(id+"F12.wireOp",EDGE,"E72.0");var subQ14=sQuery(id+"F12.wireOp",EDGE,"E72.1");var subQ16=sQuery(id+"F12.wireOp",EDGE,"E74.1");var subQ18=sQuery(id+"F12.wireOp",EDGE,"E74.8");Q0=qUnion([makeQuery(id+"F12.imprint","IMPRINT",FACE,{"disambiguationData":[TD([[makeQuery(id+"F12.imprint","IMPRINT",EDGE,{"derivedFrom":subQ7}),1.0]])]}),makeQuery(id+"F12.imprint","IMPRINT",FACE,{"disambiguationData":[TD([[makeQuery(id+"F12.imprint","IMPRINT",EDGE,{"derivedFrom":subQ14}),1.0]])]}),makeQuery(id+"F12.imprint","IMPRINT",FACE,{"disambiguationData":[TD([[makeQuery(id+"F12.imprint","IMPRINT",EDGE,{"derivedFrom":subQ16}),1.0]])]}),makeQuery(id+"F12.imprint","IMPRINT",FACE,{"disambiguationData":[TD([[makeQuery(id+"F12.imprint","IMPRINT",EDGE,{"derivedFrom":subQ18}),-1.0]])]})]);}
            var Q1;
            Q1=makeQuery(id+"F5.boolean.opBoolean","SPLIT",FACE,{"disambiguationData":[TD([makeQuery(id+"F5.opExtrude","SWEPT_FACE",FACE,{"disambiguationData":[OSD([sQuery(id+"F4.wireOp",EDGE,"E41")])]})])],"derivedFrom":makeQuery(id+"F3.boolean.opBoolean","COPY",FACE,{"derivedFrom":makeQuery(id+"F3.opExtrude","CAP_FACE",FACE,{"disambiguationData":[OSD([sQuery(id+"F0.wireOp",EDGE,"E25.0"),sQuery(id+"F0.wireOp",EDGE,"E25.1"),sQuery(id+"F0.wireOp",EDGE,"E25.2"),sQuery(id+"F0.wireOp",EDGE,"E25.3"),sQuery(id+"F0.wireOp",EDGE,"E25.4"),sQuery(id+"F0.wireOp",EDGE,"E25.5"),sQuery(id+"F0.wireOp",EDGE,"E25.6"),sQuery(id+"F0.wireOp",EDGE,"E25.7")])],"isStart":false})})});
            extrude(context, id + "F13", {"entities" : qUnion([Q0]), "operationType" : NewBodyOperationType.REMOVE, "endBound" : BoundingType.UP_TO_SURFACE, "endBoundEntityFace" : qUnion([Q1]), "depth" : 25 * mm});
        }
        {
            var Q0;
            Q0=makeQuery(id+"F3.boolean.opBoolean","COPY",EDGE,{"derivedFrom":makeQuery(id+"F3.opExtrude","CAP_EDGE",EDGE,{"disambiguationData":[OSD([sQuery(id+"F0.wireOp",EDGE,"E25.6")])],"isStart":false})});
            var Q1;
            Q1=makeQuery(id+"F8.boolean.opBoolean","INTERSECT",EDGE,{"derivedFrom":[makeQuery(id+"F5.opExtrude","SWEPT_FACE",FACE,{"disambiguationData":[OSD([sQuery(id+"F4.wireOp",EDGE,"E30")])]}),makeQuery(id+"F8.opExtrude","CAP_FACE",FACE,{"disambiguationData":[OSD([sQuery(id+"F7.wireOp",EDGE,"E67")])],"isStart":false})]});
            var Q2;
            Q2=makeQuery(id+"F8.boolean.opBoolean","INTERSECT",EDGE,{"disambiguationData":[OD(1.0)],"derivedFrom":[makeQuery(id+"F5.opExtrude","SWEPT_FACE",FACE,{"disambiguationData":[OSD([sQuery(id+"F4.wireOp",EDGE,"E30")])]}),makeQuery(id+"F8.opExtrude","SWEPT_FACE",FACE,{"disambiguationData":[OSD([sQuery(id+"F7.wireOp",EDGE,"E67")])]})]});
            var Q3;
            {var subQ0=sQuery(id+"F4.wireOp",EDGE,"E30");Q3=makeQuery(id+"F8.boolean.opBoolean","SPLIT",EDGE,{"disambiguationData":[TD([makeQuery(id+"F5.opExtrude","SWEPT_FACE",FACE,{"disambiguationData":[OSD([sQuery(id+"F4.wireOp",EDGE,"E35.filletArc")])]})])],"derivedFrom":makeQuery(id+"F5.opExtrude","CAP_EDGE",EDGE,{"disambiguationData":[OSD([subQ0])],"isStart":false})});}
            var Q4;
            {var subQ0=sQuery(id+"F0.wireOp",EDGE,"E25.7");var subQ1=sQuery(id+"F0.wireOp",EDGE,"E25.1");var subQ2=sQuery(id+"F0.wireOp",EDGE,"E25.6");var subQ3=sQuery(id+"F0.wireOp",EDGE,"E25.5");var subQ4=sQuery(id+"F0.wireOp",EDGE,"E25.4");var subQ5=sQuery(id+"F0.wireOp",EDGE,"E25.0");var subQ6=sQuery(id+"F0.wireOp",EDGE,"E25.2");var subQ7=sQuery(id+"F0.wireOp",EDGE,"E25.3");Q4=makeQuery(id+"F8.boolean.opBoolean","INTERSECT",EDGE,{"derivedFrom":[makeQuery(id+"F5.boolean.opBoolean","SPLIT",FACE,{"disambiguationData":[TD([makeQuery(id+"F2.opExtrude","SWEPT_FACE",FACE,{"disambiguationData":[OSD([subQ5])]})])],"derivedFrom":makeQuery(id+"F3.boolean.opBoolean","COPY",FACE,{"derivedFrom":makeQuery(id+"F3.opExtrude","CAP_FACE",FACE,{"disambiguationData":[OSD([subQ5,subQ1,subQ6,subQ7,subQ4,subQ3,subQ2,subQ0])],"isStart":false})})}),makeQuery(id+"F8.opExtrude","SWEPT_FACE",FACE,{"disambiguationData":[OSD([sQuery(id+"F7.wireOp",EDGE,"E67")])]})]});}
            var Q5;
            Q5=makeQuery(id+"F8.boolean.opBoolean","INTERSECT",EDGE,{"disambiguationData":[OD(0.0)],"derivedFrom":[makeQuery(id+"F5.opExtrude","SWEPT_FACE",FACE,{"disambiguationData":[OSD([sQuery(id+"F4.wireOp",EDGE,"E30")])]}),makeQuery(id+"F8.opExtrude","SWEPT_FACE",FACE,{"disambiguationData":[OSD([sQuery(id+"F7.wireOp",EDGE,"E67")])]})]});
            fillet(context, id + "F14", {"entities" : qUnion([Q0, Q1, Q2, Q3, Q4, Q5]), "radius" : 3 * mm, "tangentPropagation" : true, "allowEdgeOverflow" : false});
        }
        {
            var Q0;
            Q0=makeQuery(id+"F1.opExtrude","CAP_EDGE",EDGE,{"disambiguationData":[OSD([sQuery(id+"F0.wireOp",EDGE,"E1.bottom")])],"isStart":false});
            fillet(context, id + "F15", {"entities" : qUnion([Q0]), "radius" : 2 * mm, "tangentPropagation" : true, "allowEdgeOverflow" : false});
        }
        {
            var Q0;
            {var subQ0=sQuery(id+"F0.wireOp",EDGE,"E22.filletArc");var subQ1=sQuery(id+"F0.wireOp",EDGE,"E7");var subQ2=sQuery(id+"F0.wireOp",EDGE,"E6");var subQ3=sQuery(id+"F0.wireOp",EDGE,"E5");var subQ4=sQuery(id+"F0.wireOp",EDGE,"E4");var subQ5=sQuery(id+"F0.wireOp",EDGE,"E1.bottom");var subQ6=sQuery(id+"F0.wireOp",EDGE,"E21.filletArc");var subQ7=sQuery(id+"F0.wireOp",EDGE,"E1.top");var subQ8=sQuery(id+"F0.wireOp",EDGE,"E1.left");var subQ9=sQuery(id+"F0.wireOp",EDGE,"E1.right");var subQ10=sQuery(id+"F0.wireOp",EDGE,"E23.filletArc");var subQ11=sQuery(id+"F0.wireOp",EDGE,"E24.filletArc");Q0=makeQuery(id+"F2.boolean.opBoolean","SPLIT",FACE,{"disambiguationData":[TD([makeQuery(id+"F1.opExtrude","SWEPT_FACE",FACE,{"disambiguationData":[OSD([subQ5])]})])],"derivedFrom":makeQuery(id+"F1.opExtrude","CAP_FACE",FACE,{"disambiguationData":[OSD([subQ5,subQ7,subQ8,subQ9,subQ4,subQ3,subQ2,subQ1,subQ6,subQ0,subQ10,subQ11])],"isStart":true})});}
            var sketch = newSketch(context, id + "F16", { "sketchPlane" : qUnion([Q0])});
            skLineSegment(sketch, "E79", {"start": v(-14.1, 104.25) * mm, "end": v(-14.1, 92.25) * mm});
            skLineSegment(sketch, "E80", {"start": v(15.9, 104.25) * mm, "end": v(15.9, 92.25) * mm});
            skArc(sketch, "E81", {"start": v(15.9, 104.25) * mm, "mid": v(0.9, 119.25) * mm, "end": v(-14.1, 104.25) * mm});
            skLineSegment(sketch, "E82", {"start": v(-14.1, 92.25) * mm, "end": v(-32.1, 74.25) * mm});
            skLineSegment(sketch, "E83", {"start": v(15.9, 92.25) * mm, "end": v(33.9, 74.25) * mm});
            skCircle(sketch, "E84", {"center": v(0.9, 104.25) * mm, "radius": 6 * mm});
            skLineSegment(sketch, "E85", {"start": v(0.9, 104.25) * mm, "end": v(0.9, 74.25) * mm});
            skLineSegment(sketch, "E86", {"start": v(0, 0) * mm, "end": v(118.21, 0) * mm, "construction": true});
            skCircle(sketch, "E87.MirrorC", {"center": v(0.9, -104.25) * mm, "radius": 6 * mm});
            skArc(sketch, "E88.MirrorCS", {"start": v(15.9, -104.25) * mm, "mid": v(0.9, -119.25) * mm, "end": v(-14.1, -104.25) * mm});
            skLineSegment(sketch, "E89.MirrorCS", {"start": v(15.9, -104.25) * mm, "end": v(15.9, -92.25) * mm});
            skLineSegment(sketch, "E90.MirrorCS", {"start": v(-14.1, -104.25) * mm, "end": v(-14.1, -92.25) * mm});
            skLineSegment(sketch, "E91.MirrorCS", {"start": v(-14.1, -92.25) * mm, "end": v(-32.1, -74.25) * mm});
            skLineSegment(sketch, "E92.MirrorCS", {"start": v(15.9, -92.25) * mm, "end": v(33.9, -74.25) * mm});
            skLineSegment(sketch, "E93.MirrorCS", {"start": v(0.9, -104.25) * mm, "end": v(0.9, -74.25) * mm});
            skSolve(sketch);
        }
        {
            var Q0;
            Q0=makeQuery(id+"F16.imprint","IMPRINT",FACE,{"disambiguationData":[TD([[makeQuery(id+"F16.imprint","IMPRINT",EDGE,{"derivedFrom":makeQuery(id+"F1.opExtrude","CAP_EDGE",EDGE,{"disambiguationData":[OSD([sQuery(id+"F0.wireOp",EDGE,"E1.left")])],"isStart":true})}),-1.0]])]});
            var Q1;
            Q1=makeQuery(id+"F16.imprint","IMPRINT",FACE,{"disambiguationData":[TD([[makeQuery(id+"F16.imprint","IMPRINT",EDGE,{"derivedFrom":sQuery(id+"F16.wireOp",EDGE,"E79")}),1.0]])]});
            var Q2;
            Q2=makeQuery(id+"F16.imprint","IMPRINT",FACE,{"disambiguationData":[TD([[makeQuery(id+"F16.imprint","IMPRINT",EDGE,{"derivedFrom":sQuery(id+"F16.wireOp",EDGE,"E87.MirrorC")}),1.0]])]});
            extrude(context, id + "F17", {"entities" : qUnion([Q0, Q1, Q2]), "operationType" : NewBodyOperationType.ADD, "depth" : 25 * mm});
        }
    });
